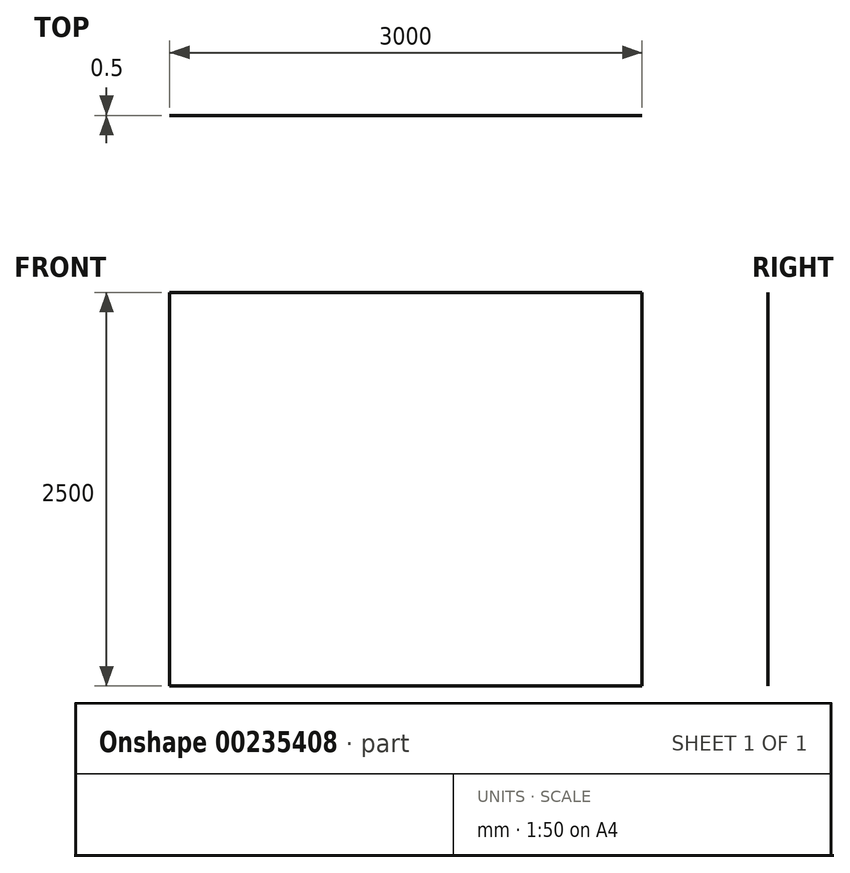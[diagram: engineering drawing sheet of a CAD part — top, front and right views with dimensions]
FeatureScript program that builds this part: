
annotation { "Feature Type Name" : "Feature", "Feature Type Description" : "" }
export const myFeature = defineFeature(function(context is Context, id is Id, definition is map)
    precondition{}
    {
        {
            var Q0;
            Q0=qCreatedBy(makeId("Front.planeOp"),FACE);
            var sketch = newSketch(context, id + "F0", { "sketchPlane" : qUnion([Q0])});
            skLineSegment(sketch, "E0.bottom", {"start": v(-720.66, 2125.17) * mm, "end": v(2279.34, 2125.17) * mm});
            skLineSegment(sketch, "E0.top", {"start": v(-720.66, -374.83) * mm, "end": v(2279.34, -374.83) * mm});
            skLineSegment(sketch, "E0.left", {"start": v(-720.66, 2125.17) * mm, "end": v(-720.66, -374.83) * mm});
            skLineSegment(sketch, "E0.right", {"start": v(2279.34, 2125.17) * mm, "end": v(2279.34, -374.83) * mm});
            skSolve(sketch);
        }
        {
            var Q0;
            Q0=makeQuery(id+"F0.imprint","IMPRINT",FACE,{"disambiguationData":[TD([[makeQuery(id+"F0.imprint","IMPRINT",EDGE,{"derivedFrom":sQuery(id+"F0.wireOp",EDGE,"E0.bottom")}),-1.0]])]});
            extrude(context, id + "F1", {"entities" : qUnion([Q0]), "depth" : 0.5 * mm});
        }
    });
